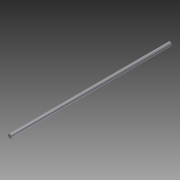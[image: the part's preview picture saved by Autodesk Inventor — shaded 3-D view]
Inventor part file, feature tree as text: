
AUTODESK INVENTOR PART (.ipt)
format: ipt  version: 2012 (Build 160160000, 160)  size: 62,464 bytes
history: native  units: in
note: dims shown in document units (in); Inventor stores cm internally (conversion verified against a paired STEP export)
features: extrude x1, sketch x1
ambient origin geometry x8: Origin, YZ Plane, XZ Plane, XY Plane, X Axis, Y Axis, Z Axis, Center Point
bodies: Solid1 (feature_tree)
feature tree (2):
  extrude  "Extrusion1"  Depth=21.25in TaperAngle=0.0deg
  sketch  "Sketch1"  dims[d0=0.5in d1=21.25in d2=0.0in]
